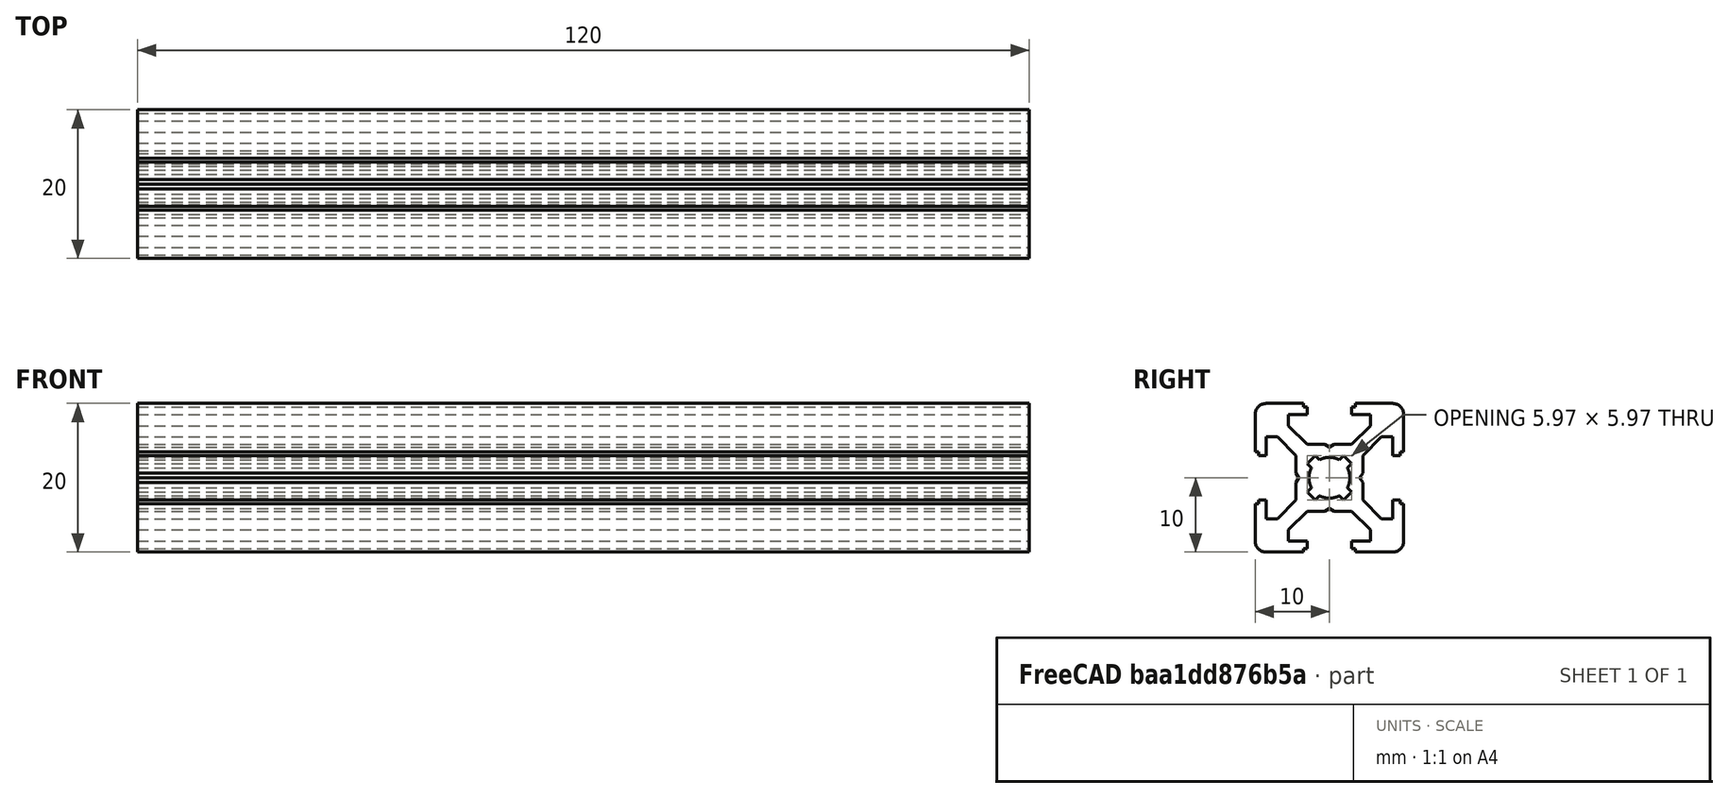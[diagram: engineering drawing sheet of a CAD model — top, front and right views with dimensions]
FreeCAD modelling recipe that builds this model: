
FCSTD DOCUMENT  (FreeCAD 0.19R)
Label: Tslot12
License: All rights reserved
LicenseURL: http://en.wikipedia.org/wiki/All_rights_reserved
objects: Sketcher::SketchObject×1, PartDesign::Pad×1, PartDesign::Body×1
note: 4 computed .brp shape members not serialized (recipe doc carries the construction recipe); baked Part::Feature solids carry a one-line shape summary decoded from their .brp

FEATURE [Sketcher::SketchObject] Sketch  label="T-Slot-Skizze"
  FullyConstrained = true
  MapMode = 5
  Placement = pos=(0,0,0) rot=(0.57735,0.57735,0.57735;2.0944rad)
  Support = -> [YZ_Plane]
  sketch-geometry (98):
    g0: LineSegment StartX=0 StartY=4.1 StartZ=0 EndX=0.65 EndY=4.5 EndZ=0
    g1: LineSegment StartX=0.65 StartY=4.5 StartZ=0 EndX=3 EndY=4.5 EndZ=0
    g2: LineSegment StartX=3 StartY=4.5 StartZ=0 EndX=5.5 EndY=7 EndZ=0
    g3: LineSegment StartX=5.5 StartY=7 StartZ=0 EndX=5.5 EndY=8.5 EndZ=0
    g4: LineSegment StartX=5.5 StartY=8.5 StartZ=0 EndX=3 EndY=8.5 EndZ=0
    g5: LineSegment StartX=3 StartY=8.5 StartZ=0 EndX=3 EndY=9.5 EndZ=0
    g6: LineSegment StartX=3 StartY=9.5 StartZ=0 EndX=3.5 EndY=9.5 EndZ=0
    g7: LineSegment StartX=3.5 StartY=9.5 StartZ=0 EndX=3.5 EndY=10 EndZ=0
    g8: LineSegment StartX=3.5 StartY=10 StartZ=0 EndX=8.5 EndY=10 EndZ=0
    g9: LineSegment StartX=10 StartY=8.5 StartZ=0 EndX=10 EndY=3.5 EndZ=0
    g10: LineSegment StartX=10 StartY=3.5 StartZ=0 EndX=9.5 EndY=3.5 EndZ=0
    g11: LineSegment StartX=9.5 StartY=3.5 StartZ=0 EndX=9.5 EndY=3 EndZ=0
    g12: LineSegment StartX=9.5 StartY=3 StartZ=0 EndX=8.5 EndY=3 EndZ=0
    g13: LineSegment StartX=8.5 StartY=3 StartZ=0 EndX=8.5 EndY=5.5 EndZ=0
    g14: LineSegment StartX=8.5 StartY=5.5 StartZ=0 EndX=7 EndY=5.5 EndZ=0
    g15: LineSegment StartX=7 StartY=5.5 StartZ=0 EndX=4.5 EndY=3 EndZ=0
    g16: LineSegment StartX=4.5 StartY=3 StartZ=0 EndX=4.5 EndY=0.65 EndZ=0
    g17: LineSegment StartX=4.5 StartY=0.65 StartZ=0 EndX=4.1 EndY=0 EndZ=0
    g18: ArcOfCircle CenterX=8.5 CenterY=8.5 CenterZ=0 NormalX=0 NormalY=0 NormalZ=1 AngleXU=0 Radius=1.5 StartAngle=0 EndAngle=1.5708
    g19: LineSegment StartX=0 StartY=-4.1 StartZ=0 EndX=0.65 EndY=-4.5 EndZ=0
    g20: LineSegment StartX=0.65 StartY=-4.5 StartZ=0 EndX=3 EndY=-4.5 EndZ=0
    g21: LineSegment StartX=3 StartY=-4.5 StartZ=0 EndX=5.5 EndY=-7 EndZ=0
    g22: LineSegment StartX=5.5 StartY=-7 StartZ=0 EndX=5.5 EndY=-8.5 EndZ=0
    g23: LineSegment StartX=5.5 StartY=-8.5 StartZ=0 EndX=3 EndY=-8.5 EndZ=0
    g24: LineSegment StartX=3 StartY=-8.5 StartZ=0 EndX=3 EndY=-9.5 EndZ=0
    g25: LineSegment StartX=3 StartY=-9.5 StartZ=0 EndX=3.5 EndY=-9.5 EndZ=0
    g26: LineSegment StartX=3.5 StartY=-9.5 StartZ=0 EndX=3.5 EndY=-10 EndZ=0
    g27: LineSegment StartX=3.5 StartY=-10 StartZ=0 EndX=8.5 EndY=-10 EndZ=0
    g28: LineSegment StartX=10 StartY=-8.5 StartZ=0 EndX=10 EndY=-3.5 EndZ=0
    g29: LineSegment StartX=10 StartY=-3.5 StartZ=0 EndX=9.5 EndY=-3.5 EndZ=0
    g30: LineSegment StartX=9.5 StartY=-3.5 StartZ=0 EndX=9.5 EndY=-3 EndZ=0
    g31: LineSegment StartX=9.5 StartY=-3 StartZ=0 EndX=8.5 EndY=-3 EndZ=0
    g32: LineSegment StartX=8.5 StartY=-3 StartZ=0 EndX=8.5 EndY=-5.5 EndZ=0
    g33: LineSegment StartX=8.5 StartY=-5.5 StartZ=0 EndX=7 EndY=-5.5 EndZ=0
    g34: LineSegment StartX=7 StartY=-5.5 StartZ=0 EndX=4.5 EndY=-3 EndZ=0
    g35: LineSegment StartX=4.5 StartY=-3 StartZ=0 EndX=4.5 EndY=-0.65 EndZ=0
    g36: ArcOfCircle CenterX=8.5 CenterY=-8.5 CenterZ=0 NormalX=0 NormalY=0 NormalZ=1 AngleXU=0 Radius=1.5 StartAngle=4.71239 EndAngle=6.28319
    g37: LineSegment StartX=4.5 StartY=-0.65 StartZ=0 EndX=4.1 EndY=0 EndZ=0
    g38: LineSegment StartX=0 StartY=-4.1 StartZ=0 EndX=-0.65 EndY=-4.5 EndZ=0
    g39: LineSegment StartX=-0.65 StartY=-4.5 StartZ=0 EndX=-3 EndY=-4.5 EndZ=0
    g40: LineSegment StartX=-3 StartY=-4.5 StartZ=0 EndX=-5.5 EndY=-7 EndZ=0
    g41: LineSegment StartX=-5.5 StartY=-7 StartZ=0 EndX=-5.5 EndY=-8.5 EndZ=0
    g42: LineSegment StartX=-5.5 StartY=-8.5 StartZ=0 EndX=-3 EndY=-8.5 EndZ=0
    g43: LineSegment StartX=-3 StartY=-8.5 StartZ=0 EndX=-3 EndY=-9.5 EndZ=0
    g44: LineSegment StartX=-3 StartY=-9.5 StartZ=0 EndX=-3.5 EndY=-9.5 EndZ=0
    g45: LineSegment StartX=-3.5 StartY=-9.5 StartZ=0 EndX=-3.5 EndY=-10 EndZ=0
    g46: LineSegment StartX=-3.5 StartY=-10 StartZ=0 EndX=-8.5 EndY=-10 EndZ=0
    g47: LineSegment StartX=-10 StartY=-8.5 StartZ=0 EndX=-10 EndY=-3.5 EndZ=0
    g48: LineSegment StartX=-10 StartY=-3.5 StartZ=0 EndX=-9.5 EndY=-3.5 EndZ=0
    g49: LineSegment StartX=-9.5 StartY=-3.5 StartZ=0 EndX=-9.5 EndY=-3 EndZ=0
    g50: LineSegment StartX=-9.5 StartY=-3 StartZ=0 EndX=-8.5 EndY=-3 EndZ=0
    g51: LineSegment StartX=-8.5 StartY=-3 StartZ=0 EndX=-8.5 EndY=-5.5 EndZ=0
    g52: LineSegment StartX=-8.5 StartY=-5.5 StartZ=0 EndX=-7 EndY=-5.5 EndZ=0
    g53: LineSegment StartX=-7 StartY=-5.5 StartZ=0 EndX=-4.5 EndY=-3 EndZ=0
    g54: LineSegment StartX=-4.5 StartY=-3 StartZ=0 EndX=-4.5 EndY=-0.65 EndZ=0
    g55: ArcOfCircle CenterX=-8.5 CenterY=-8.5 CenterZ=0 NormalX=0 NormalY=0 NormalZ=1 AngleXU=0 Radius=1.5 StartAngle=3.14159 EndAngle=4.71239
    g56: LineSegment StartX=-4.5 StartY=-0.65 StartZ=0 EndX=-4.1 EndY=0 EndZ=0
    g57: LineSegment StartX=-0.65 StartY=4.5 StartZ=0 EndX=-3 EndY=4.5 EndZ=0
    g58: LineSegment StartX=-3 StartY=4.5 StartZ=0 EndX=-5.5 EndY=7 EndZ=0
    g59: LineSegment StartX=-5.5 StartY=7 StartZ=0 EndX=-5.5 EndY=8.5 EndZ=0
    g60: LineSegment StartX=-5.5 StartY=8.5 StartZ=0 EndX=-3 EndY=8.5 EndZ=0
    g61: LineSegment StartX=-3 StartY=8.5 StartZ=0 EndX=-3 EndY=9.5 EndZ=0
    g62: LineSegment StartX=-3 StartY=9.5 StartZ=0 EndX=-3.5 EndY=9.5 EndZ=0
    g63: LineSegment StartX=-3.5 StartY=9.5 StartZ=0 EndX=-3.5 EndY=10 EndZ=0
    g64: LineSegment StartX=-3.5 StartY=10 StartZ=0 EndX=-8.5 EndY=10 EndZ=0
    g65: LineSegment StartX=-10 StartY=8.5 StartZ=0 EndX=-10 EndY=3.5 EndZ=0
    g66: LineSegment StartX=-10 StartY=3.5 StartZ=0 EndX=-9.5 EndY=3.5 EndZ=0
    g67: LineSegment StartX=-9.5 StartY=3.5 StartZ=0 EndX=-9.5 EndY=3 EndZ=0
    g68: LineSegment StartX=-9.5 StartY=3 StartZ=0 EndX=-8.5 EndY=3 EndZ=0
    g69: LineSegment StartX=-8.5 StartY=3 StartZ=0 EndX=-8.5 EndY=5.5 EndZ=0
    g70: LineSegment StartX=-8.5 StartY=5.5 StartZ=0 EndX=-7 EndY=5.5 EndZ=0
    g71: LineSegment StartX=-7 StartY=5.5 StartZ=0 EndX=-4.5 EndY=3 EndZ=0
    g72: LineSegment StartX=-4.5 StartY=3 StartZ=0 EndX=-4.5 EndY=0.65 EndZ=0
    g73: ArcOfCircle CenterX=-8.5 CenterY=8.5 CenterZ=0 NormalX=0 NormalY=0 NormalZ=1 AngleXU=0 Radius=1.5 StartAngle=1.5708 EndAngle=3.14159
    g74: LineSegment StartX=-4.5 StartY=0.65 StartZ=0 EndX=-4.1 EndY=0 EndZ=0
    g75: LineSegment StartX=0 StartY=4.1 StartZ=0 EndX=-0.65 EndY=4.5 EndZ=0
    g76: Circle CenterX=0 CenterY=0 CenterZ=0 NormalX=0 NormalY=0 NormalZ=1 AngleXU=0 Radius=3.55
    g77: Circle CenterX=0 CenterY=0 CenterZ=0 NormalX=0 NormalY=0 NormalZ=1 AngleXU=0 Radius=2.75
    g78: LineSegment StartX=1.3405 StartY=2.40116 StartZ=0 EndX=1.92324 EndY=2.9839 EndZ=0
    g79: LineSegment StartX=1.92324 StartY=2.9839 StartZ=0 EndX=2.9839 EndY=1.92324 EndZ=0
    g80: LineSegment StartX=2.9839 StartY=1.92324 StartZ=0 EndX=2.40116 EndY=1.3405 EndZ=0
    g81: ArcOfCircle CenterX=0 CenterY=0 CenterZ=0 NormalX=0 NormalY=0 NormalZ=1 AngleXU=0 Radius=2.75 StartAngle=0 EndAngle=0.509172
    g82: ArcOfCircle CenterX=0 CenterY=0 CenterZ=0 NormalX=0 NormalY=0 NormalZ=1 AngleXU=0 Radius=2.75 StartAngle=1.06162 EndAngle=1.5708
    g83: LineSegment StartX=-1.3405 StartY=2.40116 StartZ=0 EndX=-1.92324 EndY=2.9839 EndZ=0
    g84: LineSegment StartX=-1.92324 StartY=2.9839 StartZ=0 EndX=-2.9839 EndY=1.92324 EndZ=0
    g85: LineSegment StartX=-2.9839 StartY=1.92324 StartZ=0 EndX=-2.40116 EndY=1.3405 EndZ=0
    g86: ArcOfCircle CenterX=-1.3e-15 CenterY=6e-16 CenterZ=0 NormalX=0 NormalY=0 NormalZ=1 AngleXU=0 Radius=2.75 StartAngle=2.63242 EndAngle=3.14159
    g87: ArcOfCircle CenterX=-1.3e-15 CenterY=6e-16 CenterZ=0 NormalX=0 NormalY=0 NormalZ=1 AngleXU=0 Radius=2.75 StartAngle=1.5708 EndAngle=2.07997
    g88: LineSegment StartX=-1.34051 StartY=-2.40115 StartZ=0 EndX=-1.92325 EndY=-2.98389 EndZ=0
    g89: LineSegment StartX=-1.92325 StartY=-2.98389 StartZ=0 EndX=-2.9839 EndY=-1.92323 EndZ=0
    g90: LineSegment StartX=-2.9839 StartY=-1.92323 StartZ=0 EndX=-2.40116 EndY=-1.34049 EndZ=0
    g91: ArcOfCircle CenterX=-3e-16 CenterY=2e-16 CenterZ=0 NormalX=0 NormalY=0 NormalZ=1 AngleXU=0 Radius=2.75 StartAngle=3.14159 EndAngle=3.65076
    g92: ArcOfCircle CenterX=-3e-16 CenterY=2e-16 CenterZ=0 NormalX=0 NormalY=0 NormalZ=1 AngleXU=0 Radius=2.75 StartAngle=4.20321 EndAngle=4.71239
    g93: LineSegment StartX=1.34051 StartY=-2.40115 StartZ=0 EndX=1.92325 EndY=-2.98389 EndZ=0
    g94: LineSegment StartX=1.92325 StartY=-2.98389 StartZ=0 EndX=2.9839 EndY=-1.92323 EndZ=0
    g95: LineSegment StartX=2.9839 StartY=-1.92323 StartZ=0 EndX=2.40116 EndY=-1.34049 EndZ=0
    g96: ArcOfCircle CenterX=3e-16 CenterY=2e-16 CenterZ=0 NormalX=0 NormalY=0 NormalZ=1 AngleXU=0 Radius=2.75 StartAngle=4.71239 EndAngle=5.22156
    g97: ArcOfCircle CenterX=3e-16 CenterY=2e-16 CenterZ=0 NormalX=0 NormalY=0 NormalZ=1 AngleXU=0 Radius=2.75 StartAngle=5.77402 EndAngle=6.28319
  constraints (291):
    c: PointOnObject(g0,g-2)
    c: Coincident(g0,g1)
    c: Horizontal(g1)
    c: Coincident(g1,g2)
    c: Coincident(g2,g3)
    c: Vertical(g3)
    c: Coincident(g3,g4)
    c: Horizontal(g4)
    c: Coincident(g4,g5)
    c: Vertical(g5)
    c: Coincident(g5,g6)
    c: Horizontal(g6)
    c: Coincident(g6,g7)
    c: Coincident(g7,g8)
    c: Horizontal(g8)
    c: Vertical(g7)
    c: DistanceX(g-1,g5) = 3
    c: DistanceY(g4,g7) = 1.5
    c: DistanceY(g0,g7) = 5.5
    c: DistanceY(g3,g3) = 1.5
    c: DistanceY(g4,g5) = 1
    c: DistanceX(g-1,g1) = 3
    c: DistanceX(g-1,g7) = 3.5
    c: DistanceX(g0,g0) = 0.65
    c: DistanceY(g0,g0) = 0.4
    c: DistanceX(g-1,g3) = 5.5
    c: Vertical(g9)
    c: Coincident(g9,g10)
    c: Coincident(g10,g11)
    c: Coincident(g11,g12)
    c: Coincident(g12,g13)
    c: Vertical(g13)
    c: Coincident(g13,g14)
    c: Horizontal(g14)
    c: Coincident(g14,g15)
    c: Coincident(g15,g16)
    c: Vertical(g16)
    c: Coincident(g16,g17)
    c: PointOnObject(g17,g-1)
    c: Horizontal(g10)
    c: Horizontal(g12)
    c: Vertical(g11)
    c: Equal(g17,g0)
    c: Equal(g1,g16)
    c: Equal(g15,g2)
    c: Equal(g3,g14)
    c: Equal(g13,g4)
    c: Equal(g12,g5)
    c: Parallel(g15,g2)
    c: Equal(g11,g6)
    c: Equal(g10,g7)
    c: Equal(g9,g8)
    c: Tangent(g8,g18) = 1.5708
    c: Tangent(g9,g18) = 1.5708
    c: Radius(g18) = 1.5
    c: DistanceY(g-1,g8) = 10
    c: DistanceX(g-1,g9) = 10
    c: Coincident(g19,g20)
    c: Horizontal(g20)
    c: Coincident(g20,g21)
    c: Coincident(g21,g22)
    c: Vertical(g22)
    c: Coincident(g22,g23)
    c: Horizontal(g23)
    c: Coincident(g23,g24)
    c: Vertical(g24)
    c: Coincident(g24,g25)
    c: Horizontal(g25)
    c: Coincident(g25,g26)
    c: Coincident(g26,g27)
    c: Horizontal(g27)
    c: Vertical(g26)
    c: Vertical(g28)
    c: Coincident(g28,g29)
    c: Coincident(g29,g30)
    c: Coincident(g30,g31)
    c: Coincident(g31,g32)
    c: Vertical(g32)
    c: Coincident(g32,g33)
    c: Horizontal(g33)
    c: Coincident(g33,g34)
    c: Coincident(g34,g35)
    c: Vertical(g35)
    c: Coincident(g35,g37)
    c: Horizontal(g29)
    c: Horizontal(g31)
    c: Vertical(g30)
    c: Equal(g37,g19)
    c: Equal(g20,g35)
    c: Equal(g34,g21)
    c: Equal(g22,g33)
    c: Equal(g32,g23)
    c: Equal(g31,g24)
    c: Parallel(g34,g21)
    c: Equal(g30,g25)
    c: Equal(g29,g26)
    c: Equal(g28,g27)
    c: Tangent(g27,g36) = -1.5708
    c: Tangent(g28,g36) = -1.5708
    c: Radius(g36) = 1.5
    c: Equal(g9,g28)
    c: Equal(g12,g31)
    c: DistanceX(g-1,g28) = 10
    c: DistanceY(g27,g-1) = 10
    c: DistanceY(g30,g-1) = 3
    c: Equal(g33,g14)
    c: Equal(g35,g16)
    c: Equal(g17,g37)
    c: Coincident(g37,g17)
    c: Equal(g15,g34)
    c: PointOnObject(g19,g-2)
    c: DistanceY(g34,g-1) = 3
    c: DistanceX(g-1,g20) = 3
    c: Coincident(g38,g39)
    c: Horizontal(g39)
    c: Coincident(g39,g40)
    c: Coincident(g40,g41)
    c: Vertical(g41)
    c: Coincident(g41,g42)
    c: Horizontal(g42)
    c: Coincident(g42,g43)
    c: Vertical(g43)
    c: Coincident(g43,g44)
    c: Horizontal(g44)
    c: Coincident(g44,g45)
    c: Coincident(g45,g46)
    c: Horizontal(g46)
    c: Vertical(g45)
    c: Vertical(g47)
    c: Coincident(g47,g48)
    c: Coincident(g48,g49)
    c: Coincident(g49,g50)
    c: Coincident(g50,g51)
    c: Vertical(g51)
    c: Coincident(g51,g52)
    c: Horizontal(g52)
    c: Coincident(g52,g53)
    c: Coincident(g53,g54)
    c: Vertical(g54)
    c: Coincident(g54,g56)
    c: Horizontal(g48)
    c: Horizontal(g50)
    c: Vertical(g49)
    c: Equal(g39,g54)
    c: Equal(g53,g40)
    c: Equal(g41,g52)
    c: Equal(g51,g42)
    c: Equal(g50,g43)
    c: Parallel(g53,g40)
    c: Equal(g49,g44)
    c: Equal(g48,g45)
    c: Equal(g47,g46)
    c: Tangent(g46,g55) = 1.5708
    c: Tangent(g47,g55) = 1.5708
    c: Radius(g55) = 1.5
    c: Coincident(g38,g19)
    c: DistanceX(g39,g-1) = 3
    c: DistanceX(g38,g19) = 0.65
    c: DistanceY(g38,g19) = 0.4
    c: PointOnObject(g56,g-1)
    c: Equal(g56,g38)
    c: DistanceY(g53,g-1) = 3
    c: Equal(g22,g41)
    c: Equal(g42,g23)
    c: Equal(g24,g43)
    c: Equal(g25,g44)
    c: Equal(g26,g45)
    c: DistanceY(g46,g-1) = 10
    c: DistanceX(g47,g-1) = 10
    c: Coincident(g75,g57)
    c: Horizontal(g57)
    c: Coincident(g57,g58)
    c: Coincident(g58,g59)
    c: Vertical(g59)
    c: Coincident(g59,g60)
    c: Horizontal(g60)
    c: Coincident(g60,g61)
    c: Vertical(g61)
    c: Coincident(g61,g62)
    c: Horizontal(g62)
    c: Coincident(g62,g63)
    c: Coincident(g63,g64)
    c: Horizontal(g64)
    c: Vertical(g63)
    c: Vertical(g65)
    c: Coincident(g65,g66)
    c: Coincident(g66,g67)
    c: Coincident(g67,g68)
    c: Coincident(g68,g69)
    c: Vertical(g69)
    c: Coincident(g69,g70)
    c: Horizontal(g70)
    c: Coincident(g70,g71)
    c: Coincident(g71,g72)
    c: Vertical(g72)
    c: Coincident(g72,g74)
    c: Horizontal(g66)
    c: Horizontal(g68)
    c: Vertical(g67)
    c: Equal(g57,g72)
    c: Equal(g71,g58)
    c: Equal(g59,g70)
    c: Equal(g69,g60)
    c: Equal(g68,g61)
    c: Parallel(g71,g58)
    c: Equal(g67,g62)
    c: Equal(g66,g63)
    c: Equal(g65,g64)
    c: Tangent(g64,g73) = -1.5708
    c: Tangent(g65,g73) = -1.5708
    c: Radius(g73) = 1.5
    c: Equal(g74,g75)
    c: Coincident(g56,g74)
    c: Coincident(g0,g75)
    c: Equal(g0,g75)
    c: Equal(g1,g57)
    c: Equal(g2,g58)
    c: Equal(g3,g59)
    c: Equal(g4,g60)
    c: Equal(g5,g61)
    c: Equal(g6,g62)
    c: Equal(g7,g63)
    c: Equal(g8,g64)
    c: DistanceX(g65,g-1) = 10
    c: Coincident(g76,g-1)
    c: Coincident(g77,g-1)
    c: Radius(g76) = 3.55
    c: Radius(g77) = 2.75
    c: PointOnObject(g78,g77)
    c: PointOnObject(g78,g76)
    c: Coincident(g78,g79)
    c: PointOnObject(g79,g76)
    c: Coincident(g79,g80)
    c: PointOnObject(g80,g77)
    c: Coincident(g81,g-1)
    c: Coincident(g81,g80)
    c: Coincident(g82,g81)
    c: Coincident(g82,g78)
    c: Parallel(g78,g80)
    c: Parallel(g78,g2)
    c: Distance(g79) = 1.5
    c: Distance(g78,g80) = 1.5
    c: PointOnObject(g82,g-2)
    c: PointOnObject(g81,g-1)
    c: Coincident(g83,g84)
    c: Coincident(g84,g85)
    c: Coincident(g86,g85)
    c: Coincident(g87,g86)
    c: Coincident(g87,g83)
    c: Parallel(g83,g85)
    c: Distance(g84) = 1.5
    c: Distance(g83,g85) = 1.5
    c: Coincident(g82,g87)
    c: PointOnObject(g86,g-1)
    c: PointOnObject(g83,g76)
    c: PointOnObject(g83,g77)
    c: PointOnObject(g85,g77)
    c: PointOnObject(g84,g76)
    c: PointOnObject(g86,g77)
    c: Parallel(g85,g71)
    c: Coincident(g88,g89)
    c: Coincident(g89,g90)
    c: Coincident(g91,g90)
    c: Coincident(g92,g91)
    c: Coincident(g92,g88)
    c: Parallel(g88,g90)
    c: Distance(g89) = 1.5
    c: Distance(g88,g90) = 1.5
    c: PointOnObject(g88,g77)
    c: PointOnObject(g90,g77)
    c: Coincident(g86,g91)
    c: PointOnObject(g89,g76)
    c: PointOnObject(g88,g76)
    c: PointOnObject(g92,g-2)
    c: PointOnObject(g92,g77)
    c: Parallel(g88,g40)
    c: Coincident(g93,g94)
    c: Coincident(g94,g95)
    c: Coincident(g97,g95)
    c: Coincident(g96,g97)
    c: Coincident(g96,g93)
    c: Parallel(g93,g95)
    c: Distance(g94) = 1.5
    c: Distance(g93,g95) = 1.5
    c: Coincident(g81,g97)
    c: Coincident(g92,g96)
    c: PointOnObject(g93,g77)
    c: PointOnObject(g95,g77)
    c: PointOnObject(g94,g76)
    c: PointOnObject(g93,g76)
    c: Parallel(g93,g21)
FEATURE [PartDesign::Pad] Pad  label="T-Slot-Element"
  Direction = (1,1,1)
  Length = 120
  Length2 = 100
  Placement = pos=(0,0,0) rot=(0.57735,0.57735,0.57735;2.0944rad)
  Profile = -> Sketch
  Type = 0
FEATURE [PartDesign::Body] Body  label="T-Slot-Profil 20x20"
  Group = -> [Sketch,Pad]
  Origin = -> Origin
  Tip = -> Pad
